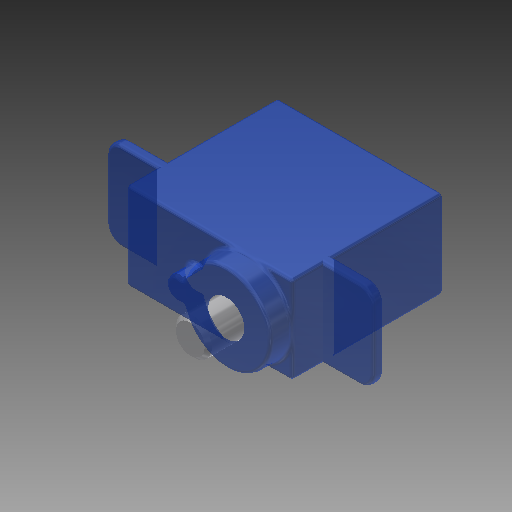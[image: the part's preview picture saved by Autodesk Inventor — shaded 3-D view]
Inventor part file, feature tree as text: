
AUTODESK INVENTOR PART (.ipt)
format: ipt  version: 2018 (Build 220112000, 112)  size: 313,344 bytes
history: native  units: mm
features: extrude x4, sketch x4, fillet x3, plane x1, chamfer x1, projected_geometry x1
ambient origin geometry x8: Origin, YZ Plane, XZ Plane, XY Plane, X Axis, Y Axis, Z Axis, Center Point
bodies: Solid1 (feature_tree)
feature tree (14):
  extrude  "Extrusion1"  Depth=12.2mm
  extrude  "Extrusion2"  Depth=29.0mm
  extrude  "Extrusion3"  Depth=3.0mm
  plane  "Work Plane1"
  extrude  "Extrusion4"  Depth=5.0mm
  fillet  "Fillet1"  Radius=5.0mm
  fillet  "Fillet2"  [1 undecoded]
  fillet  "Fillet3"  Radius=12.2mm
  chamfer  "Chamfer1"  Distance=7.0mm
  sketch  "Sketch1"  dims[d0=23.0mm d1=12.2mm]
  sketch  "Sketch2"  dims[d2=29.0mm d3=0.0mm d4=6.9mm]
  sketch  "Sketch3"  dims[d5=3.0mm d6=6.1mm]
  sketch  "Sketch4"  dims[d7=8.0mm d8=0.0mm d9=5.0mm d10=5.0mm d11=0.0mm d12=-5.0mm d13=12.2mm d14=7.0mm d15=7.0mm d16=1.5mm d17=0.0mm d18=0.5mm d19=2.0mm d20=0.5mm d21=0.5mm d22=2.0mm d23=45.0deg]
  projected_geometry  "Projected Loop1"
note: 1 required parameter value undecoded (feature->parameter linkage not recoverable at this tier; creation-order binding heuristic only, values carry confidence <= 0.55)
